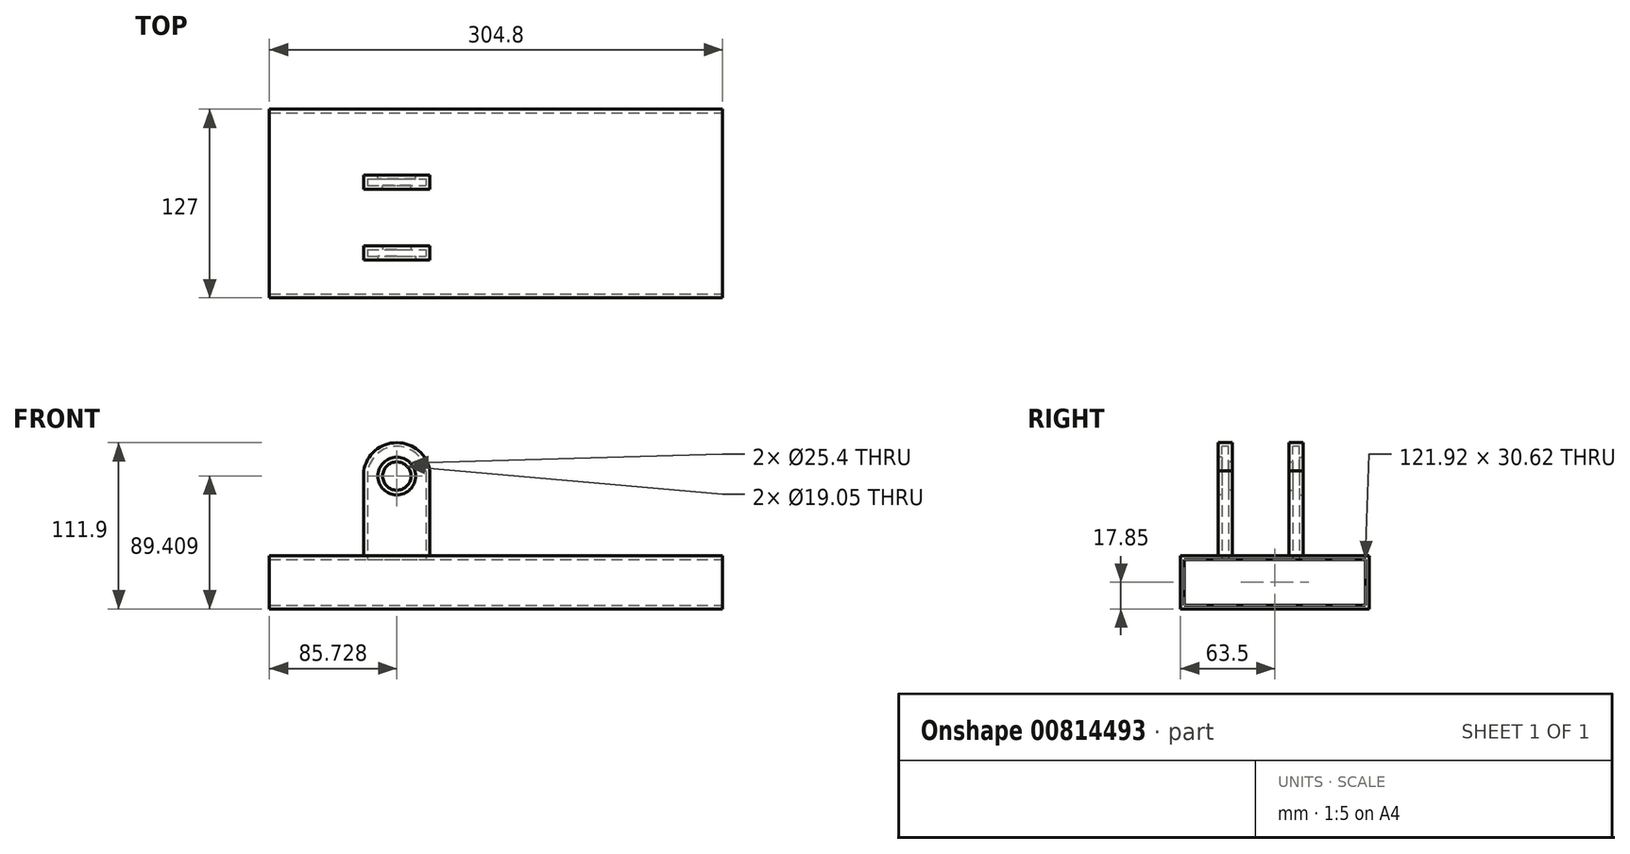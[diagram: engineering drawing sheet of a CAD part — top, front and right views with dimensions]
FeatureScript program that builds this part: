
annotation { "Feature Type Name" : "Feature", "Feature Type Description" : "" }
export const myFeature = defineFeature(function(context is Context, id is Id, definition is map)
    precondition{}
    {
        {
            var Q0;
            Q0=qCreatedBy(makeId("Front.planeOp"),FACE);
            var sketch = newSketch(context, id + "F0", { "sketchPlane" : qUnion([Q0])});
            skLineSegment(sketch, "E0.bottom", {"start": v(-126.94, -29.27) * mm, "end": v(177.86, -29.27) * mm});
            skLineSegment(sketch, "E0.top", {"start": v(-126.94, -64.97) * mm, "end": v(177.86, -64.97) * mm});
            skLineSegment(sketch, "E0.left", {"start": v(-126.94, -29.27) * mm, "end": v(-126.94, -64.97) * mm});
            skLineSegment(sketch, "E0.right", {"start": v(177.86, -29.27) * mm, "end": v(177.86, -64.97) * mm});
            skSolve(sketch);
        }
        {
            var Q0;
            Q0=makeQuery(id+"F0.imprint","IMPRINT",FACE,{"disambiguationData":[TD([[makeQuery(id+"F0.imprint","IMPRINT",EDGE,{"derivedFrom":sQuery(id+"F0.wireOp",EDGE,"E0.bottom")}),-1.0]])]});
            extrude(context, id + "F1", {"entities" : qUnion([Q0]), "endBound" : BoundingType.SYMMETRIC, "depth" : 127 * mm, "offsetDistance" : 25.4 * mm});
        }
        {
            var Q0;
            Q0=makeQuery(id+"F1.opExtrude","CAP_FACE",FACE,{"disambiguationData":[OSD([sQuery(id+"F0.wireOp",EDGE,"E0.bottom"),sQuery(id+"F0.wireOp",EDGE,"E0.top"),sQuery(id+"F0.wireOp",EDGE,"E0.left"),sQuery(id+"F0.wireOp",EDGE,"E0.right")])],"isStart":false});
            var sketch = newSketch(context, id + "F2", { "sketchPlane" : qUnion([Q0])});
            skLineSegment(sketch, "E1.bottom", {"start": v(-62.55, 15.18) * mm, "end": v(-37.15, 15.18) * mm});
            skLineSegment(sketch, "E1.top", {"start": v(-62.55, -29.27) * mm, "end": v(-37.15, -29.27) * mm});
            skLineSegment(sketch, "E1.left", {"start": v(-62.55, 15.18) * mm, "end": v(-62.55, -29.27) * mm});
            skLineSegment(sketch, "E1.right", {"start": v(-37.15, 15.18) * mm, "end": v(-37.15, -29.27) * mm});
            skArc(sketch, "E2", {"start": v(-37.15, 15.18) * mm, "mid": v(-49.85, 27.88) * mm, "end": v(-62.55, 15.18) * mm});
            skSolve(sketch);
        }
        {
            var Q0;
            Q0 = qSketchRegion(id + "F2", true);
            extrude(context, id + "F3", {"entities" : qUnion([Q0]), "operationType" : NewBodyOperationType.REMOVE, "depth" : -152.4 * mm, "offsetDistance" : 25.4 * mm});
        }
        {
            var Q0;
            Q0=makeQuery(id+"F1.opExtrude","SWEPT_FACE",FACE,{"disambiguationData":[OSD([sQuery(id+"F0.wireOp",EDGE,"E0.bottom")])]});
            var sketch = newSketch(context, id + "F4", { "sketchPlane" : qUnion([Q0])});
            skLineSegment(sketch, "E3.bottom", {"start": v(-63.44, 19.05) * mm, "end": v(-18.99, 19.05) * mm});
            skLineSegment(sketch, "E3.top", {"start": v(-63.44, 9.52) * mm, "end": v(-18.99, 9.52) * mm});
            skLineSegment(sketch, "E3.left", {"start": v(-63.44, 19.05) * mm, "end": v(-63.44, 9.52) * mm});
            skLineSegment(sketch, "E3.right", {"start": v(-18.99, 19.05) * mm, "end": v(-18.99, 9.52) * mm});
            skLineSegment(sketch, "E4.bottom", {"start": v(-63.44, -28.57) * mm, "end": v(-18.99, -28.57) * mm});
            skLineSegment(sketch, "E4.top", {"start": v(-63.44, -38.1) * mm, "end": v(-18.99, -38.1) * mm});
            skLineSegment(sketch, "E4.left", {"start": v(-63.44, -28.57) * mm, "end": v(-63.44, -38.1) * mm});
            skLineSegment(sketch, "E4.right", {"start": v(-18.99, -28.57) * mm, "end": v(-18.99, -38.1) * mm});
            skSolve(sketch);
        }
        {
            var Q0;
            Q0=makeQuery(id+"F4.imprint","IMPRINT",FACE,{"disambiguationData":[TD([[makeQuery(id+"F4.imprint","IMPRINT",EDGE,{"derivedFrom":sQuery(id+"F4.wireOp",EDGE,"E3.bottom")}),-1.0]])]});
            extrude(context, id + "F5", {"entities" : qUnion([Q0]), "operationType" : NewBodyOperationType.ADD, "depth" : 57.15 * mm, "offsetDistance" : 25.4 * mm});
        }
        {
            var Q0;
            Q0 = qSketchRegion(id + "F4", true);
            extrude(context, id + "F6", {"entities" : qUnion([Q0]), "operationType" : NewBodyOperationType.ADD, "depth" : 57.15 * mm, "offsetDistance" : 25.4 * mm});
        }
        {
            var Q0;
            Q0=makeQuery(id+"F6.opExtrude","SWEPT_FACE",FACE,{"disambiguationData":[OSD([sQuery(id+"F4.wireOp",EDGE,"E4.top")])]});
            var sketch = newSketch(context, id + "F7", { "sketchPlane" : qUnion([Q0])});
            skArc(sketch, "E5", {"start": v(-18.99, 27.88) * mm, "mid": v(-41.21, 46.93) * mm, "end": v(-63.44, 27.88) * mm});
            skSolve(sketch);
        }
        {
            var Q0;
            Q0=makeQuery(id+"F5.opExtrude","SWEPT_FACE",FACE,{"disambiguationData":[OSD([sQuery(id+"F4.wireOp",EDGE,"E3.top")])]});
            var sketch = newSketch(context, id + "F8", { "sketchPlane" : qUnion([Q0])});
            skArc(sketch, "E6", {"start": v(-18.99, 27.88) * mm, "mid": v(-41.21, 46.93) * mm, "end": v(-63.44, 27.88) * mm});
            skSolve(sketch);
        }
        {
            var Q0;
            Q0=makeQuery(id+"F7.imprint","IMPRINT",FACE,{"disambiguationData":[TD([[makeQuery(id+"F7.imprint","IMPRINT",EDGE,{"derivedFrom":sQuery(id+"F7.wireOp",EDGE,"E5")}),1.0]])]});
            extrude(context, id + "F9", {"entities" : qUnion([Q0]), "operationType" : NewBodyOperationType.ADD, "depth" : -9.52 * mm, "offsetDistance" : 25.4 * mm});
        }
        {
            var Q0;
            Q0=makeQuery(id+"F8.imprint","IMPRINT",FACE,{"disambiguationData":[TD([[makeQuery(id+"F8.imprint","IMPRINT",EDGE,{"derivedFrom":sQuery(id+"F8.wireOp",EDGE,"E6")}),1.0]])]});
            extrude(context, id + "F10", {"entities" : qUnion([Q0]), "operationType" : NewBodyOperationType.ADD, "depth" : -9.52 * mm, "offsetDistance" : 25.4 * mm});
        }
        {
            var Q0;
            Q0=makeQuery(id+"F1.opExtrude","SWEPT_FACE",FACE,{"disambiguationData":[OSD([sQuery(id+"F0.wireOp",EDGE,"E0.top")])]});
            var sketch = newSketch(context, id + "F11", { "sketchPlane" : qUnion([Q0])});
            skLineSegment(sketch, "E7.bottom", {"start": v(-126.94, 57.79) * mm, "end": v(177.86, 57.79) * mm});
            skLineSegment(sketch, "E7.top", {"start": v(-126.94, -56.51) * mm, "end": v(177.86, -56.51) * mm});
            skLineSegment(sketch, "E7.left", {"start": v(-126.94, 57.79) * mm, "end": v(-126.94, -56.51) * mm});
            skLineSegment(sketch, "E7.right", {"start": v(177.86, 57.79) * mm, "end": v(177.86, -56.51) * mm});
            skSolve(sketch);
        }
        {
            var Q0;
            Q0=makeQuery(id+"F11.imprint","IMPRINT",FACE,{"disambiguationData":[TD([[makeQuery(id+"F11.imprint","IMPRINT",EDGE,{"derivedFrom":sQuery(id+"F11.wireOp",EDGE,"E7.bottom")}),-1.0]])]});
            extrude(context, id + "F12", {"entities" : qUnion([Q0]), "operationType" : NewBodyOperationType.ADD, "depth" : -31.75 * mm, "offsetDistance" : 25.4 * mm});
        }
        {
            var Q0;
            Q0=makeQuery(id+"F1.opExtrude","SWEPT_FACE",FACE,{"disambiguationData":[OSD([sQuery(id+"F0.wireOp",EDGE,"E0.left")])]});
            var Q1;
            Q1=makeQuery(id+"F1.opExtrude","SWEPT_FACE",FACE,{"disambiguationData":[OSD([sQuery(id+"F0.wireOp",EDGE,"E0.right")])]});
            shell(context, id + "F13", {"entities" : qUnion([Q0, Q1]), "thickness" : 2.54 * mm});
        }
        {
            var Q0;
            {var subQ0=sQuery(id+"F4.wireOp",EDGE,"E4.top");Q0=makeQuery(id+"F9.boolean.opBoolean","MERGE",FACE,{"derivedFrom":[makeQuery(id+"F6.opExtrude","SWEPT_FACE",FACE,{"disambiguationData":[OSD([subQ0])]}),makeQuery(id+"F9.opExtrude","CAP_FACE",FACE,{"disambiguationData":[OSD([subQ0,sQuery(id+"F7.wireOp",EDGE,"E5")])],"isStart":true})]});}
            var sketch = newSketch(context, id + "F14", { "sketchPlane" : qUnion([Q0])});
            skCircle(sketch, "E8", {"center": v(-41.21, 24.44) * mm, "radius": 9.53 * mm});
            skSolve(sketch);
        }
        {
            var Q0;
            Q0=makeQuery(id+"F10.boolean.opBoolean","MERGE",FACE,{"derivedFrom":[makeQuery(id+"F5.opExtrude","SWEPT_FACE",FACE,{"disambiguationData":[OSD([sQuery(id+"F4.wireOp",EDGE,"E3.bottom")])]}),makeQuery(id+"F10.opExtrude","CAP_FACE",FACE,{"disambiguationData":[OSD([sQuery(id+"F4.wireOp",EDGE,"E3.top"),sQuery(id+"F8.wireOp",EDGE,"E6")])],"isStart":false})]});
            var sketch = newSketch(context, id + "F15", { "sketchPlane" : qUnion([Q0])});
            skCircle(sketch, "E9", {"center": v(41.21, 24.44) * mm, "radius": 9.53 * mm});
            skSolve(sketch);
        }
        {
            var Q0;
            Q0=sQuery(id+"F14.wireOp",VERTEX,"E8.center");
            var Q1;
            Q1=makeQuery(id+"F1.opExtrude","SWEPT_BODY",BODY,{"disambiguationData":[OSD([sQuery(id+"F0.wireOp",EDGE,"E0.bottom"),sQuery(id+"F0.wireOp",EDGE,"E0.top"),sQuery(id+"F0.wireOp",EDGE,"E0.left"),sQuery(id+"F0.wireOp",EDGE,"E0.right")])]});
            hole(context, id + "F16", {"style" : HoleStyle.C_BORE, "endStyle" : HoleEndStyle.BLIND, "holeDiameter" : 19.05 * mm, "cBoreDiameter" : 25.4 * mm, "cBoreDepth" : 3.8 * mm, "majorDiameter" : 6.35 * mm, "holeDepth" : 9.52 * mm, "isTappedThrough" : true, "tappedDepth" : 12.7 * mm, "tapClearance" : 3, "startFromSketch" : true, "locations" : qUnion([Q0]), "scope" : qUnion([Q1])});
        }
        {
            var Q0;
            Q0=sQuery(id+"F15.wireOp",VERTEX,"E9.center");
            var Q1;
            Q1=makeQuery(id+"F1.opExtrude","SWEPT_BODY",BODY,{"disambiguationData":[OSD([sQuery(id+"F0.wireOp",EDGE,"E0.bottom"),sQuery(id+"F0.wireOp",EDGE,"E0.top"),sQuery(id+"F0.wireOp",EDGE,"E0.left"),sQuery(id+"F0.wireOp",EDGE,"E0.right")])]});
            hole(context, id + "F17", {"style" : HoleStyle.C_BORE, "endStyle" : HoleEndStyle.BLIND, "holeDiameter" : 19.05 * mm, "cBoreDiameter" : 25.4 * mm, "cBoreDepth" : 3.8 * mm, "majorDiameter" : 6.35 * mm, "holeDepth" : 9.52 * mm, "isTappedThrough" : true, "tappedDepth" : 12.7 * mm, "tapClearance" : 3, "startFromSketch" : true, "locations" : qUnion([Q0]), "scope" : qUnion([Q1])});
        }
    });
